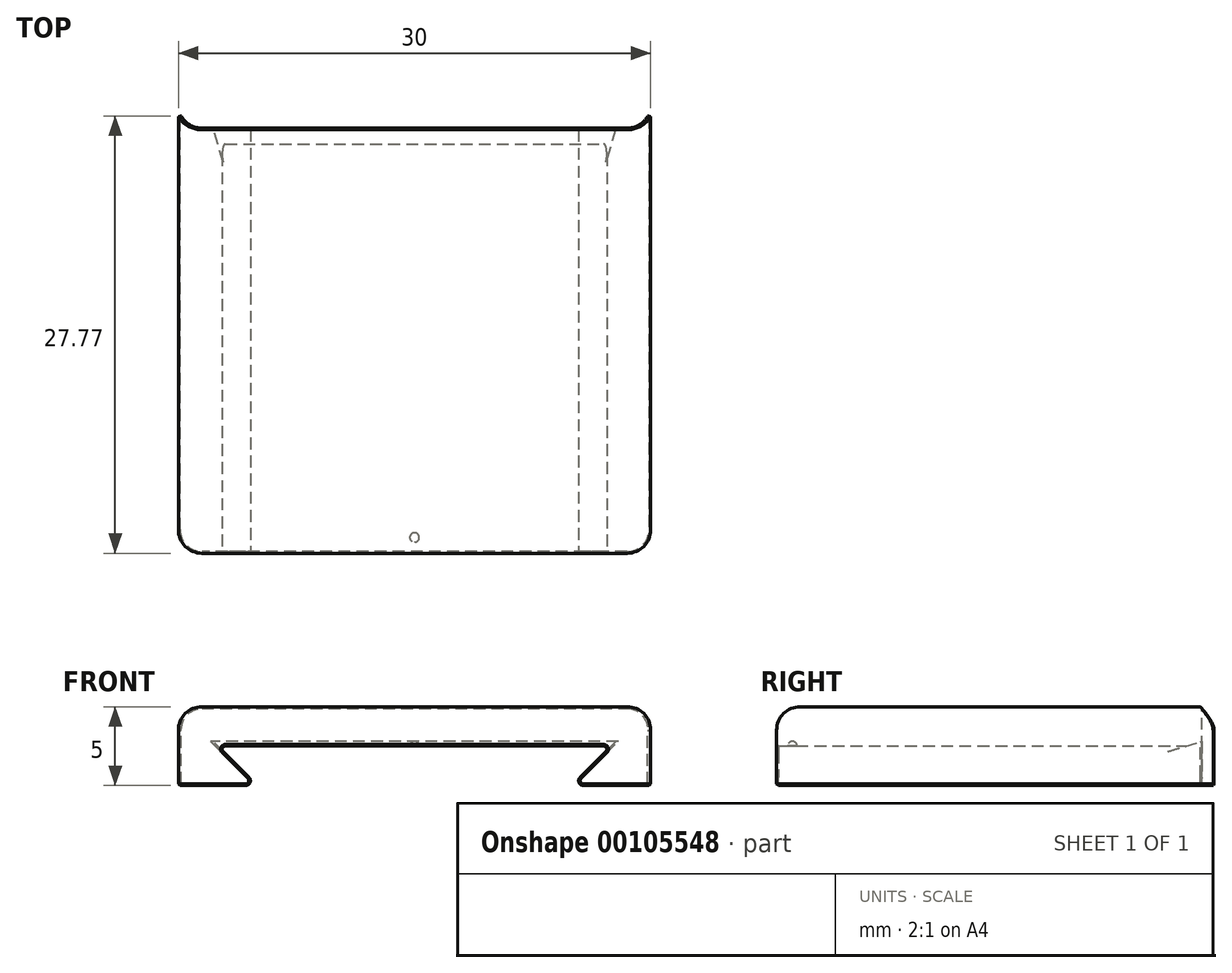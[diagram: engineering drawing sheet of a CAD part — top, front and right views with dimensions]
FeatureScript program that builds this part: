
annotation { "Feature Type Name" : "Feature", "Feature Type Description" : "" }
export const myFeature = defineFeature(function(context is Context, id is Id, definition is map)
    precondition{}
    {
        {
            var Q0;
            Q0=qCreatedBy(makeId("Front.planeOp"),FACE);
            var sketch = newSketch(context, id + "F0", { "sketchPlane" : qUnion([Q0])});
            skLineSegment(sketch, "E0.bottom", {"start": v(15, 2.5) * mm, "end": v(-15, 2.5) * mm});
            skLineSegment(sketch, "E0.top", {"start": v(15, -2.5) * mm, "end": v(-15, -2.5) * mm});
            skLineSegment(sketch, "E0.left", {"start": v(15, 2.5) * mm, "end": v(15, -2.5) * mm});
            skLineSegment(sketch, "E0.right", {"start": v(-15, 2.5) * mm, "end": v(-15, -2.5) * mm});
            skPoint(sketch, "E0.middle", {"position": v(0, 0) * mm});
            skLineSegment(sketch, "E1", {"start": v(-10, -2.5) * mm, "end": v(-12.5, 0) * mm});
            skLineSegment(sketch, "E2", {"start": v(-12.5, 0) * mm, "end": v(12.5, 0) * mm});
            skLineSegment(sketch, "E3", {"start": v(12.5, 0) * mm, "end": v(10, -2.5) * mm});
            skSolve(sketch);
        }
        {
            var Q0;
            Q0=makeQuery(id+"F0.imprint","IMPRINT",FACE,{"disambiguationData":[TD([[makeQuery(id+"F0.imprint","IMPRINT",EDGE,{"derivedFrom":sQuery(id+"F0.wireOp",EDGE,"E0.bottom")}),1.0]])]});
            extrude(context, id + "F1", {"entities" : qUnion([Q0]), "endBound" : BoundingType.SYMMETRIC, "depth" : 27 * mm});
        }
        {
            var Q0;
            Q0=makeQuery(id+"F1.opExtrude","CAP_EDGE",EDGE,{"disambiguationData":[OSD([sQuery(id+"F0.wireOp",EDGE,"E2")])],"isStart":true});
            chamfer(context, id + "F2", {"entities" : qUnion([Q0]), "chamferType" : ChamferType.TWO_OFFSETS, "width1" : 1 * mm, "oppositeDirection" : false, "width2" : 0.3 * mm, "tangentPropagation" : true});
        }
        {
            var Q0;
            Q0=makeQuery(id+"F1.opExtrude","SWEPT_EDGE",EDGE,{"disambiguationData":[OSD([sQuery(id+"F0.wireOp",EDGE,"E2"),sQuery(id+"F0.wireOp",EDGE,"E3")])]});
            var Q1;
            Q1=makeQuery(id+"F1.opExtrude","SWEPT_EDGE",EDGE,{"disambiguationData":[OSD([sQuery(id+"F0.wireOp",EDGE,"E1"),sQuery(id+"F0.wireOp",EDGE,"E2")])]});
            fillet(context, id + "F3", {"entities" : qUnion([Q0, Q1]), "radius" : 0.2 * mm, "tangentPropagation" : true, "allowEdgeOverflow" : false});
        }
        {
            var Q0;
            Q0=makeQuery(id+"F1.opExtrude","SWEPT_EDGE",EDGE,{"disambiguationData":[OSD([sQuery(id+"F0.wireOp",EDGE,"E0.top"),sQuery(id+"F0.wireOp",EDGE,"E3")])]});
            var Q1;
            Q1=makeQuery(id+"F1.opExtrude","SWEPT_EDGE",EDGE,{"disambiguationData":[OSD([sQuery(id+"F0.wireOp",EDGE,"E0.top"),sQuery(id+"F0.wireOp",EDGE,"E1")])]});
            fillet(context, id + "F4", {"entities" : qUnion([Q0, Q1]), "radius" : 0.3 * mm, "tangentPropagation" : true, "allowEdgeOverflow" : false});
        }
        {
            var Q0;
            Q0=makeQuery(id+"F1.opExtrude","SWEPT_FACE",FACE,{"disambiguationData":[OSD([sQuery(id+"F0.wireOp",EDGE,"E0.bottom")])]});
            var sketch = newSketch(context, id + "F5", { "sketchPlane" : qUnion([Q0])});
            skLineSegment(sketch, "E4", {"start": v(15, 13.5) * mm, "end": v(15, 15) * mm});
            skLineSegment(sketch, "E5", {"start": v(-15, 13.5) * mm, "end": v(-15, 15) * mm});
            skArc(sketch, "E6", {"start": v(-15, 15) * mm, "mid": v(-14.56, 13.94) * mm, "end": v(-13.5, 13.5) * mm});
            skArc(sketch, "E7", {"start": v(15, 15) * mm, "mid": v(14.56, 13.94) * mm, "end": v(13.5, 13.5) * mm});
            skSolve(sketch);
        }
        {
            var Q0;
            {var subQ0=sQuery(id+"F5.wireOp",EDGE,"E5");Q0=makeQuery(id+"F5.imprint","IMPRINT",FACE,{"disambiguationData":[TD([[makeQuery(id+"F5.imprint","IMPRINT",EDGE,{"derivedFrom":subQ0}),-1.0]])]});}
            var Q1;
            {var subQ0=sQuery(id+"F5.wireOp",EDGE,"E4");Q1=makeQuery(id+"F5.imprint","IMPRINT",FACE,{"disambiguationData":[TD([[makeQuery(id+"F5.imprint","IMPRINT",EDGE,{"derivedFrom":subQ0}),1.0]])]});}
            extrude(context, id + "F6", {"entities" : qUnion([Q0, Q1]), "operationType" : NewBodyOperationType.ADD, "oppositeDirection" : true, "depth" : 5 * mm});
        }
        {
            var Q0;
            Q0=makeQuery(id+"F1.opExtrude","CAP_EDGE",EDGE,{"disambiguationData":[OSD([sQuery(id+"F0.wireOp",EDGE,"E0.right")])],"isStart":false});
            var Q1;
            Q1=makeQuery(id+"F1.opExtrude","CAP_EDGE",EDGE,{"disambiguationData":[OSD([sQuery(id+"F0.wireOp",EDGE,"E0.left")])],"isStart":false});
            var Q2;
            Q2=makeQuery(id+"F1.opExtrude","SWEPT_EDGE",EDGE,{"disambiguationData":[OSD([sQuery(id+"F0.wireOp",EDGE,"E0.bottom"),sQuery(id+"F0.wireOp",EDGE,"E0.right")])]});
            var Q3;
            Q3=makeQuery(id+"F1.opExtrude","CAP_EDGE",EDGE,{"disambiguationData":[OSD([sQuery(id+"F0.wireOp",EDGE,"E0.bottom")])],"isStart":false});
            var Q4;
            Q4=makeQuery(id+"F1.opExtrude","SWEPT_EDGE",EDGE,{"disambiguationData":[OSD([sQuery(id+"F0.wireOp",EDGE,"E0.bottom"),sQuery(id+"F0.wireOp",EDGE,"E0.left")])]});
            var Q5;
            Q5=makeQuery(id+"F6.opExtrude","CAP_EDGE",EDGE,{"disambiguationData":[OSD([sQuery(id+"F5.wireOp",EDGE,"E4")])],"isStart":true});
            var Q6;
            Q6=makeQuery(id+"F6.opExtrude","CAP_EDGE",EDGE,{"disambiguationData":[OSD([sQuery(id+"F5.wireOp",EDGE,"E5")])],"isStart":true});
            fillet(context, id + "F7", {"entities" : qUnion([Q0, Q1, Q2, Q3, Q4, Q5, Q6]), "radius" : 1.5 * mm, "tangentPropagation" : true, "allowEdgeOverflow" : false});
        }
        {
            var Q0;
            Q0=makeQuery(id+"F1.opExtrude","SWEPT_EDGE",EDGE,{"disambiguationData":[OSD([sQuery(id+"F0.wireOp",EDGE,"E0.top"),sQuery(id+"F0.wireOp",EDGE,"E0.right")])]});
            var Q1;
            Q1=makeQuery(id+"F1.opExtrude","SWEPT_EDGE",EDGE,{"disambiguationData":[OSD([sQuery(id+"F0.wireOp",EDGE,"E0.top"),sQuery(id+"F0.wireOp",EDGE,"E0.left")])]});
            var Q2;
            {var subQ0=sQuery(id+"F0.wireOp",EDGE,"E0.top");Q2=makeQuery(id+"F1.opExtrude","CAP_EDGE",EDGE,{"disambiguationData":[OSD([subQ0]),TDD([makeQuery(id+"F0.imprint","IMPRINT",EDGE,{"disambiguationData":[TD([[makeQuery(id+"F0.imprint","INTERSECT",VERTEX,{"derivedFrom":[subQ0,sQuery(id+"F0.wireOp",EDGE,"E0.right")]}),1.0]])],"derivedFrom":subQ0})])],"isStart":false});}
            var Q3;
            Q3=makeQuery(id+"F1.opExtrude","CAP_EDGE",EDGE,{"disambiguationData":[OSD([sQuery(id+"F0.wireOp",EDGE,"E0.bottom")])],"isStart":true});
            var Q4;
            {var subQ0=sQuery(id+"F0.wireOp",EDGE,"E0.top");Q4=makeQuery(id+"F1.opExtrude","CAP_EDGE",EDGE,{"disambiguationData":[OSD([subQ0]),TDD([makeQuery(id+"F0.imprint","IMPRINT",EDGE,{"disambiguationData":[TD([[makeQuery(id+"F0.imprint","INTERSECT",VERTEX,{"derivedFrom":[subQ0,sQuery(id+"F0.wireOp",EDGE,"E0.left")]}),-1.0]])],"derivedFrom":subQ0})])],"isStart":true});}
            var Q5;
            {var subQ0=sQuery(id+"F0.wireOp",EDGE,"E0.top");Q5=makeQuery(id+"F1.opExtrude","CAP_EDGE",EDGE,{"disambiguationData":[OSD([subQ0]),TDD([makeQuery(id+"F0.imprint","IMPRINT",EDGE,{"disambiguationData":[TD([[makeQuery(id+"F0.imprint","INTERSECT",VERTEX,{"derivedFrom":[subQ0,sQuery(id+"F0.wireOp",EDGE,"E0.right")]}),1.0]])],"derivedFrom":subQ0})])],"isStart":true});}
            chamfer(context, id + "F8", {"entities" : qUnion([Q0, Q1, Q2, Q3, Q4, Q5]), "width" : 0.1 * mm, "tangentPropagation" : true});
        }
        {
            var Q0;
            Q0=makeQuery(id+"F1.opExtrude","SWEPT_FACE",FACE,{"disambiguationData":[OSD([sQuery(id+"F0.wireOp",EDGE,"E2")])]});
            var sketch = newSketch(context, id + "F9", { "sketchPlane" : qUnion([Q0])});
            skCircle(sketch, "E8", {"center": v(0, 12.5) * mm, "radius": 0.3 * mm});
            skLineSegment(sketch, "E9", {"start": v(0, 12.8) * mm, "end": v(0, 12.2) * mm});
            skSolve(sketch);
        }
        {
            var Q0;
            {var subQ0=sQuery(id+"F9.wireOp",EDGE,"E9");Q0=makeQuery(id+"F9.imprint","IMPRINT",FACE,{"disambiguationData":[TD([[makeQuery(id+"F9.imprint","IMPRINT",EDGE,{"derivedFrom":subQ0}),-1.0]])]});}
            var Q1;
            Q1=sQuery(id+"F9.wireOp",EDGE,"E9");
            revolve(context, id + "F10", {"operationType" : NewBodyOperationType.REMOVE, "entities" : qUnion([Q0]), "axis" : qUnion([Q1]), "revolveType" : RevolveType.FULL, "oppositeDirection" : true});
        }
    });
